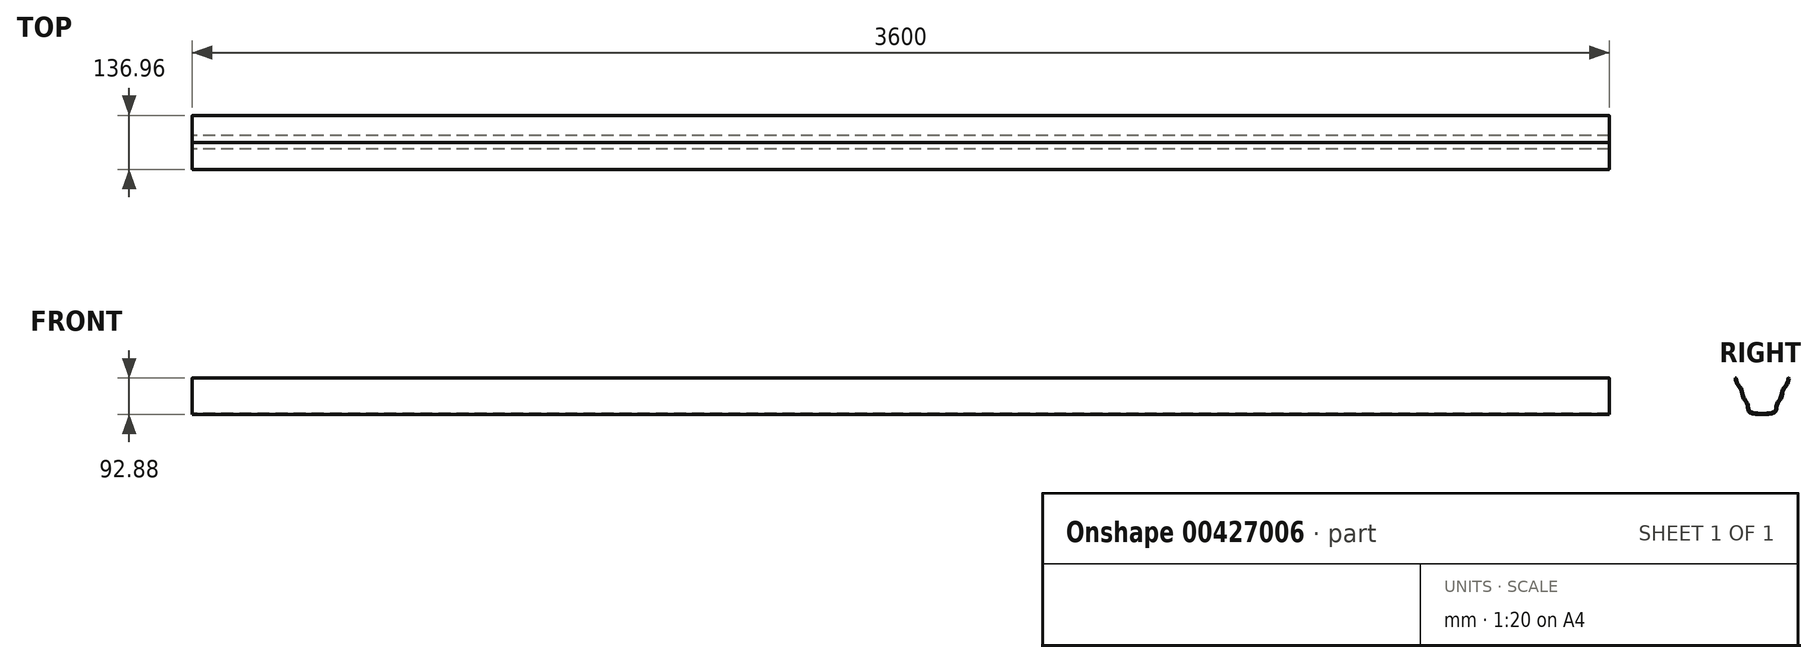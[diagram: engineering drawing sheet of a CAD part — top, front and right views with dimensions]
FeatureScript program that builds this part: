
annotation { "Feature Type Name" : "Feature", "Feature Type Description" : "" }
export const myFeature = defineFeature(function(context is Context, id is Id, definition is map)
    precondition{}
    {
        {
            var Q0;
            Q0=qCreatedBy(makeId("Right.planeOp"),FACE);
            var sketch = newSketch(context, id + "F0", { "sketchPlane" : qUnion([Q0])});
            skPoint(sketch, "E0.visualSharp", {"position": v(-120, 0) * mm});
            skPoint(sketch, "E1.start.orphan", {"position": v(-75, 100) * mm});
            skPoint(sketch, "E2.visualSharp", {"position": v(-6.04, 102.86) * mm});
            skPoint(sketch, "E3.visualSharp", {"position": v(-10.5, 102.86) * mm});
            skPoint(sketch, "E4.visualSharp", {"position": v(-11.4, 100) * mm});
            skPoint(sketch, "E5.visualSharp", {"position": v(-13.5, 100) * mm});
            skPoint(sketch, "E6.visualSharp", {"position": v(-13.5, 105.86) * mm});
            skPoint(sketch, "E7.visualSharp", {"position": v(0, 105.86) * mm});
            skFitSpline(sketch, "E8.0", {"points": [v(-6.54, 100.08) * mm, v(-6.77, 98.71) * mm, v(-7.28, 95.97) * mm, v(-8.25, 91.96) * mm, v(-9.3, 88.8) * mm, v(-10.34, 86.42) * mm, v(-11.23, 84.72) * mm, v(-12.24, 83.13) * mm, v(-13.73, 81.1) * mm, v(-15.77, 78.63) * mm, v(-17.8, 76.06) * mm, v(-19.27, 73.8) * mm, v(-20.25, 71.97) * mm, v(-21.07, 69.97) * mm, v(-21.96, 67.13) * mm, v(-22.82, 63.34) * mm, v(-23.59, 59.42) * mm, v(-24.3, 56.33) * mm, v(-24.92, 54.08) * mm, v(-25.53, 52.27) * mm, v(-26.1, 50.88) * mm, v(-26.73, 49.54) * mm, v(-27.62, 47.93) * mm, v(-28.81, 46.07) * mm, v(-30.09, 44.26) * mm, v(-31.39, 42.47) * mm, v(-32.67, 40.67) * mm, v(-33.88, 38.82) * mm, v(-34.98, 36.9) * mm, v(-35.74, 35.2) * mm, v(-36.25, 33.79) * mm, v(-36.66, 32.32) * mm, v(-37.03, 30.42) * mm, v(-37.34, 28.09) * mm, v(-37.7, 24.96) * mm, v(-38.28, 21.12) * mm, v(-39.59, 17.7) * mm, v(-41.41, 15.35) * mm, v(-43.88, 13.3) * mm, v(-48.46, 11.35) * mm, v(-55.7, 9.88) * mm, v(-64.02, 9.14) * mm, v(-72.8, 8.94) * mm, v(-79.97, 9.08) * mm, v(-85.32, 9.28) * mm, v(-89.06, 9.45) * mm, v(-92.44, 9.63) * mm, v(-95.4, 9.79) * mm, v(-97.85, 9.9) * mm, v(-99.74, 9.94) * mm, v(-101.2, 9.95) * mm, v(-102.31, 9.92) * mm, v(-103.2, 9.9) * mm, v(-103.7, 9.87) * mm, v(-103.96, 9.87) * mm]});
            skFitSpline(sketch, "E8.1", {"points": [v(-143.46, 100.08) * mm, v(-143.23, 98.71) * mm, v(-142.72, 95.97) * mm, v(-141.75, 91.96) * mm, v(-140.7, 88.8) * mm, v(-139.66, 86.42) * mm, v(-138.77, 84.72) * mm, v(-137.76, 83.13) * mm, v(-136.27, 81.1) * mm, v(-134.23, 78.63) * mm, v(-132.2, 76.06) * mm, v(-130.73, 73.8) * mm, v(-129.75, 71.97) * mm, v(-128.93, 69.97) * mm, v(-128.04, 67.13) * mm, v(-127.18, 63.34) * mm, v(-126.41, 59.42) * mm, v(-125.7, 56.33) * mm, v(-125.08, 54.08) * mm, v(-124.47, 52.27) * mm, v(-123.9, 50.88) * mm, v(-123.27, 49.54) * mm, v(-122.38, 47.93) * mm, v(-121.19, 46.07) * mm, v(-119.91, 44.26) * mm, v(-118.61, 42.47) * mm, v(-117.33, 40.67) * mm, v(-116.12, 38.82) * mm, v(-115.02, 36.9) * mm, v(-114.26, 35.2) * mm, v(-113.75, 33.79) * mm, v(-113.34, 32.32) * mm, v(-112.97, 30.42) * mm, v(-112.66, 28.09) * mm, v(-112.3, 24.96) * mm, v(-111.72, 21.12) * mm, v(-110.41, 17.7) * mm, v(-108.59, 15.35) * mm, v(-106.12, 13.3) * mm, v(-101.54, 11.35) * mm, v(-94.3, 9.88) * mm, v(-85.98, 9.14) * mm, v(-77.2, 8.94) * mm, v(-70.03, 9.08) * mm, v(-64.68, 9.28) * mm, v(-60.94, 9.45) * mm, v(-57.56, 9.63) * mm, v(-54.6, 9.79) * mm, v(-52.15, 9.9) * mm, v(-50.26, 9.94) * mm, v(-48.8, 9.95) * mm, v(-47.69, 9.92) * mm, v(-46.8, 9.9) * mm, v(-46.3, 9.87) * mm, v(-46.04, 9.87) * mm]});
            skFitSpline(sketch, "E9.0", {"points": [v(-9.5, 100.59) * mm, v(-9.72, 99.24) * mm, v(-10.22, 96.58) * mm, v(-10.98, 93.4) * mm, v(-11.73, 91.02) * mm, v(-12.35, 89.32) * mm, v(-12.94, 87.98) * mm, v(-13.45, 86.96) * mm, v(-13.84, 86.24) * mm, v(-14.27, 85.53) * mm, v(-14.88, 84.6) * mm, v(-15.74, 83.44) * mm, v(-16.87, 82) * mm, v(-18.1, 80.51) * mm, v(-19.36, 78.93) * mm, v(-20.42, 77.5) * mm, v(-21.24, 76.27) * mm, v(-21.84, 75.31) * mm, v(-22.4, 74.3) * mm, v(-22.95, 73.22) * mm, v(-23.44, 72.1) * mm, v(-24.02, 70.59) * mm, v(-24.63, 68.65) * mm, v(-25.23, 66.3) * mm, v(-25.75, 63.93) * mm, v(-26.22, 61.58) * mm, v(-26.7, 59.28) * mm, v(-27.21, 57.06) * mm, v(-27.7, 55.3) * mm, v(-28.12, 53.96) * mm, v(-28.47, 53) * mm, v(-28.85, 52.08) * mm, v(-29.4, 50.92) * mm, v(-30.19, 49.48) * mm, v(-31.3, 47.76) * mm, v(-32.52, 46.02) * mm, v(-33.82, 44.23) * mm, v(-35.14, 42.37) * mm, v(-36.44, 40.4) * mm, v(-37.45, 38.63) * mm, v(-38.17, 37.12) * mm, v(-38.59, 36.13) * mm, v(-38.89, 35.32) * mm, v(-39.1, 34.7) * mm, v(-39.29, 34.06) * mm, v(-39.52, 33.2) * mm, v(-39.75, 32.15) * mm, v(-40.05, 30.48) * mm, v(-40.32, 28.44) * mm, v(-40.6, 26.1) * mm, v(-40.9, 23.9) * mm, v(-41.3, 21.91) * mm, v(-41.86, 20.18) * mm, v(-42.6, 18.7) * mm, v(-43.42, 17.67) * mm, v(-44.25, 16.9) * mm, v(-44.99, 16.36) * mm, v(-45.9, 15.82) * mm, v(-46.97, 15.3) * mm, v(-48.21, 14.82) * mm, v(-50.05, 14.21) * mm, v(-52.68, 13.56) * mm, v(-56.25, 12.95) * mm, v(-60.13, 12.5) * mm, v(-65.6, 12.1) * mm, v(-72.8, 11.94) * mm, v(-79.89, 12.08) * mm, v(-85.2, 12.28) * mm, v(-88.9, 12.45) * mm, v(-92.28, 12.63) * mm, v(-95.25, 12.78) * mm, v(-97.32, 12.87) * mm, v(-98.72, 12.92) * mm, v(-99.95, 12.94) * mm, v(-101.22, 12.95) * mm, v(-102.4, 12.92) * mm, v(-103.32, 12.89) * mm, v(-103.79, 12.87) * mm, v(-104, 12.87) * mm]});
            skFitSpline(sketch, "E9.1", {"points": [v(-140.5, 100.59) * mm, v(-140.28, 99.24) * mm, v(-139.78, 96.58) * mm, v(-139.02, 93.4) * mm, v(-138.27, 91.02) * mm, v(-137.65, 89.32) * mm, v(-137.06, 87.98) * mm, v(-136.55, 86.96) * mm, v(-136.16, 86.24) * mm, v(-135.73, 85.53) * mm, v(-135.12, 84.6) * mm, v(-134.26, 83.44) * mm, v(-133.13, 82) * mm, v(-131.9, 80.51) * mm, v(-130.64, 78.93) * mm, v(-129.58, 77.5) * mm, v(-128.76, 76.27) * mm, v(-128.16, 75.31) * mm, v(-127.6, 74.3) * mm, v(-127.05, 73.22) * mm, v(-126.56, 72.1) * mm, v(-125.98, 70.59) * mm, v(-125.37, 68.65) * mm, v(-124.77, 66.3) * mm, v(-124.25, 63.93) * mm, v(-123.78, 61.58) * mm, v(-123.3, 59.28) * mm, v(-122.79, 57.06) * mm, v(-122.3, 55.3) * mm, v(-121.88, 53.96) * mm, v(-121.53, 53) * mm, v(-121.15, 52.08) * mm, v(-120.6, 50.92) * mm, v(-119.81, 49.48) * mm, v(-118.7, 47.76) * mm, v(-117.48, 46.02) * mm, v(-116.18, 44.23) * mm, v(-114.86, 42.37) * mm, v(-113.56, 40.4) * mm, v(-112.55, 38.63) * mm, v(-111.83, 37.12) * mm, v(-111.41, 36.13) * mm, v(-111.11, 35.32) * mm, v(-110.9, 34.7) * mm, v(-110.71, 34.06) * mm, v(-110.48, 33.2) * mm, v(-110.25, 32.15) * mm, v(-109.95, 30.48) * mm, v(-109.68, 28.44) * mm, v(-109.4, 26.1) * mm, v(-109.1, 23.9) * mm, v(-108.7, 21.91) * mm, v(-108.14, 20.18) * mm, v(-107.4, 18.7) * mm, v(-106.58, 17.67) * mm, v(-105.75, 16.9) * mm, v(-105.01, 16.36) * mm, v(-104.1, 15.82) * mm, v(-103.03, 15.3) * mm, v(-101.79, 14.82) * mm, v(-99.95, 14.21) * mm, v(-97.32, 13.56) * mm, v(-93.75, 12.95) * mm, v(-89.87, 12.5) * mm, v(-84.4, 12.1) * mm, v(-77.2, 11.94) * mm, v(-70.11, 12.08) * mm, v(-64.8, 12.28) * mm, v(-61.1, 12.45) * mm, v(-57.72, 12.63) * mm, v(-54.75, 12.78) * mm, v(-52.68, 12.87) * mm, v(-51.28, 12.92) * mm, v(-50.05, 12.94) * mm, v(-48.78, 12.95) * mm, v(-47.6, 12.92) * mm, v(-46.68, 12.89) * mm, v(-46.21, 12.87) * mm, v(-46, 12.87) * mm]});
            skArc(sketch, "E10", {"start": v(-143.46, 100.08) * mm, "mid": v(-142.24, 101.81) * mm, "end": v(-140.5, 100.59) * mm});
            skArc(sketch, "E11", {"start": v(-9.5, 100.59) * mm, "mid": v(-7.76, 101.81) * mm, "end": v(-6.54, 100.08) * mm});
            skPoint(sketch, "E12.1.internal.orphan", {"position": v(-143.96, 102.15) * mm});
            skPoint(sketch, "E12.4.internal.orphan", {"position": v(-136, 100) * mm});
            skPoint(sketch, "E12.9.internal.orphan", {"position": v(-143.96, 107.02) * mm});
            skPoint(sketch, "E13.start.orphan", {"position": v(-150, 100) * mm});
            skPoint(sketch, "E14.start.orphan", {"position": v(-143.96, 100) * mm});
            skPoint(sketch, "E15.end.orphan", {"position": v(0, 100) * mm});
            skPoint(sketch, "E16.start.orphan", {"position": v(-6.04, 100) * mm});
            skSolve(sketch);
        }
        {
            var Q0;
            Q0=makeQuery(id+"F0.imprint","IMPRINT",FACE,{"disambiguationData":[TD([[makeQuery(id+"F0.imprint","IMPRINT",EDGE,{"derivedFrom":sQuery(id+"F0.wireOp",EDGE,"E8.0")}),-1.0]])]});
            extrude(context, id + "F1", {"entities" : qUnion([Q0]), "depth" : 3600 * mm});
        }
    });
